# Revit family: Valve-Globe-Cla_Val-B90GE_01LFS-Flanged-SI--
name_source: partatom
category: Pipe Accessories
units: mm (PartAtom-declared; Revit-internal decimal feet)

## family parameters
Always vertical = Yes
Cut with Voids When Loaded = No
Part Type = Valve - Breaks Into
Round Connector Dimension = Use Diameter
Shared = No
Work Plane-Based = No

## types (1)
- ERROR_LOAD TYPE CATALOG
    Assembly Code = D2090
    Body Material = Metal - CLA-VAL - Ductile Iron - Red
    CV (liters per second) = 8
    Connection Axis to Side Ports = 37 mm
    Connection Axis to Upper Cover Flange = 70 mm  [stored 0.229659 ft]
    Connection Axis to Valve Top = 140 mm  [stored 0.459318 ft]
    Connection Radius = 20 mm
    Connection Size = 40 mm
    Connection Type = Flanged
    Connection to Connection = 215 mm  [stored 0.705381 ft]
    Cover Port Center Offset = 30 mm  [stored 0.0984252 ft]
    Default Elevation = 0 mm  [stored 0 ft]
    Description = Pressure Reducing Valve
    ENGworks Global = http://www.ENGworksGlobal.com
    Flange Outside Radius = 75 mm  [stored 0.246063 ft]
    Flow Configuration = In/Out
    Four Port Cover = No
    K Coefficient = 0.373067
    K Coefficient Table = Globe Valve Flanged
    Kv Coefficient = 109.633493
    Loss Method = K Coefficient
    Manufacturer = Cla-Val
    Maximum Flow Rate = 8.000 L/s
    Maximum Flow Rate Value = 8
    Maximum Operating Temperature = 65 °C
    Maximum Working Pressure = 16 bar
    Minimum Flow Rate = 0.000 L/s
    Minimum Flow Rate Value = 0
    Minimum Operating Temperature = 0 °C
    Model = B90GE-01/LFS
    Pilot System Offset = 90 mm
    Pilot System Pipe Diameter = 10 mm
    Pilot System Pipe Radius = 5 mm
    Pipe Angle Offset = 26 mm
    Product Page URL = https://www.cla-val.co.uk
    Series = Pressure Reducing Valve
    Side Ports Horizontal Offset = 51 mm  [stored 0.167323 ft]
    Standards = ASTM A536, B16.42
    Tick Size = 124 mm
    Top Port Vertical Offset = 18 mm
    Two Port Cover = Yes
    URL = https://www.cla-val.co.uk
    Unit Weight = 13 kgf
    Unit Weight Value = 13
    Version = 1
    X Pilot System Offset = 252 mm  [stored 0.826772 ft]
    Y Pilot System Offset = 145 mm  [stored 0.475722 ft]
    Z Pilot System Offset = 150 mm  [stored 0.492126 ft]

note: [stored X ft] marks values corroborated as IEEE doubles in the binary element streams (Revit-internal decimal feet)

## geometry (parser evidence)
native form markers: Sweep x9
no freeform markers — native parametric forms only
